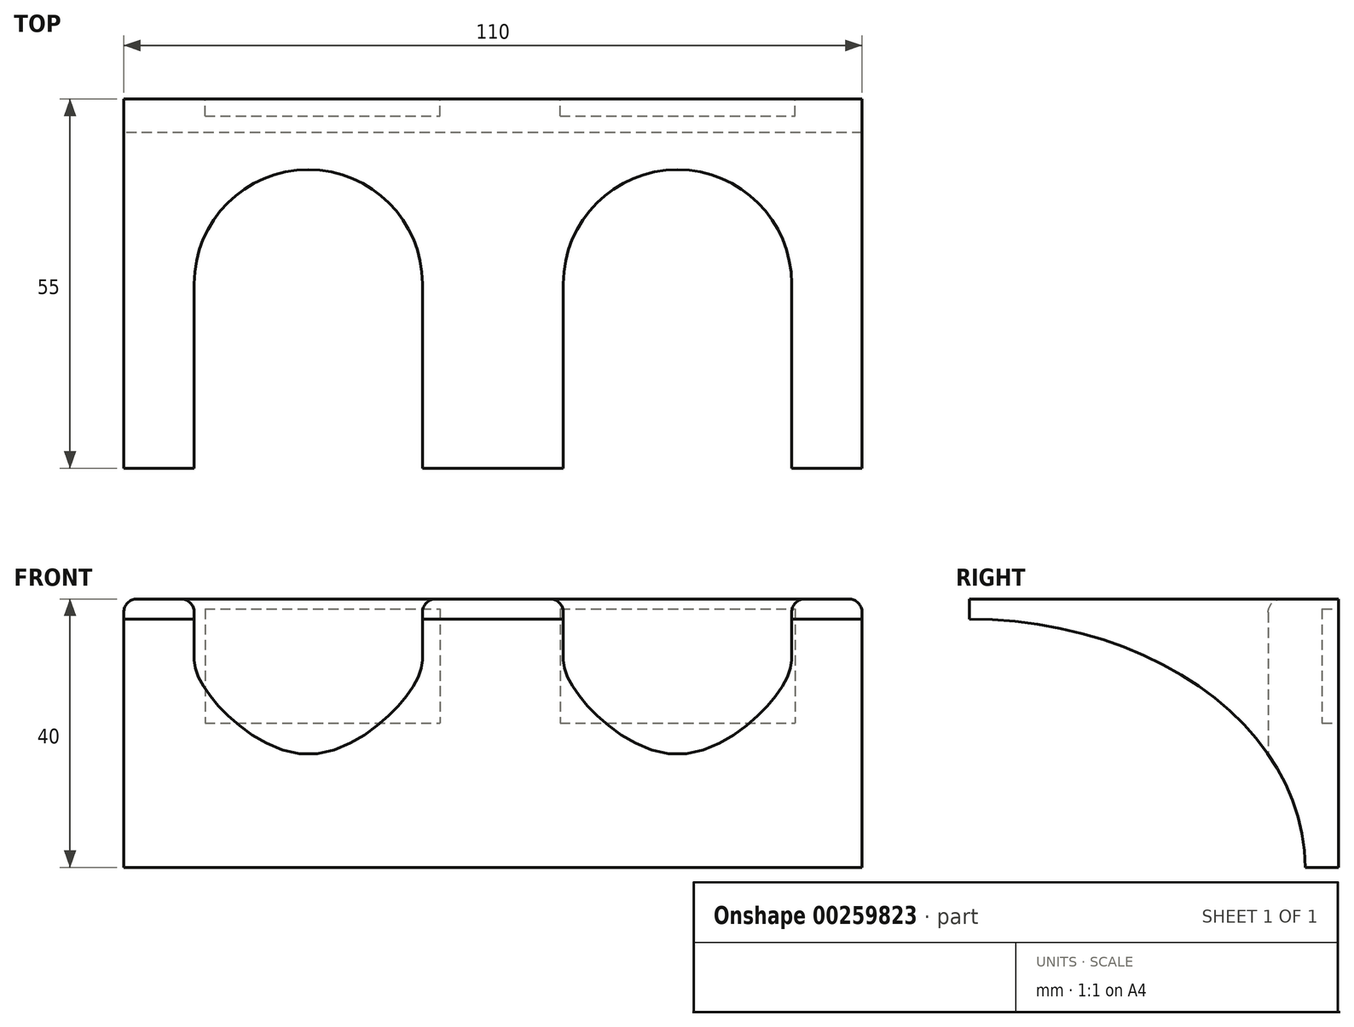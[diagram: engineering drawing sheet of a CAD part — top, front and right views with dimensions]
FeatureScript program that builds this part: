
annotation { "Feature Type Name" : "Feature", "Feature Type Description" : "" }
export const myFeature = defineFeature(function(context is Context, id is Id, definition is map)
    precondition{}
    {
        {
            var Q0;
            Q0=qCreatedBy(makeId("Top.planeOp"),FACE);
            var sketch = newSketch(context, id + "F0", { "sketchPlane" : qUnion([Q0])});
            skLineSegment(sketch, "E0.bottom", {"start": v(55, 27.5) * mm, "end": v(-55, 27.5) * mm});
            skLineSegment(sketch, "E0.top", {"start": v(55, -27.5) * mm, "end": v(-55, -27.5) * mm});
            skLineSegment(sketch, "E0.left", {"start": v(55, 27.5) * mm, "end": v(55, -27.5) * mm});
            skLineSegment(sketch, "E0.right", {"start": v(-55, 27.5) * mm, "end": v(-55, -27.5) * mm});
            skPoint(sketch, "E0.middle", {"position": v(0, 0) * mm});
            skLineSegment(sketch, "E1", {"start": v(0, 0) * mm, "end": v(-55, 0) * mm});
            skLineSegment(sketch, "E2", {"start": v(0, 0) * mm, "end": v(55, 0) * mm});
            skCircle(sketch, "E3", {"center": v(-27.5, 0) * mm, "radius": 17 * mm});
            skCircle(sketch, "E4", {"center": v(27.5, 0) * mm, "radius": 17 * mm});
            skLineSegment(sketch, "E5", {"start": v(-44.5, 0) * mm, "end": v(-44.5, -27.5) * mm});
            skLineSegment(sketch, "E6", {"start": v(-10.5, 0) * mm, "end": v(-10.5, -27.5) * mm});
            skLineSegment(sketch, "E7", {"start": v(10.5, 0) * mm, "end": v(10.5, -27.5) * mm});
            skLineSegment(sketch, "E8", {"start": v(44.5, 0) * mm, "end": v(44.5, -27.5) * mm});
            skSolve(sketch);
        }
        {
            var Q0;
            {var subQ3=sQuery(id+"F0.wireOp",EDGE,"E5");Q0=makeQuery(id+"F0.imprint","IMPRINT",FACE,{"disambiguationData":[TD([[makeQuery(id+"F0.imprint","IMPRINT",EDGE,{"derivedFrom":subQ3}),-1.0]])]});}
            var Q1;
            {var subQ6=sQuery(id+"F0.wireOp",EDGE,"E0.bottom");Q1=makeQuery(id+"F0.imprint","IMPRINT",FACE,{"disambiguationData":[TD([[makeQuery(id+"F0.imprint","IMPRINT",EDGE,{"derivedFrom":subQ6}),1.0]])]});}
            var Q2;
            {var subQ0=sQuery(id+"F0.wireOp",EDGE,"E6");Q2=makeQuery(id+"F0.imprint","IMPRINT",FACE,{"disambiguationData":[TD([[makeQuery(id+"F0.imprint","IMPRINT",EDGE,{"derivedFrom":subQ0}),1.0]])]});}
            var Q3;
            {var subQ3=sQuery(id+"F0.wireOp",EDGE,"E8");Q3=makeQuery(id+"F0.imprint","IMPRINT",FACE,{"disambiguationData":[TD([[makeQuery(id+"F0.imprint","IMPRINT",EDGE,{"derivedFrom":subQ3}),1.0]])]});}
            extrude(context, id + "F1", {"entities" : qUnion([Q0, Q1, Q2, Q3]), "depth" : 40 * mm});
        }
        {
            var Q0;
            Q0=makeQuery(id+"F1.opExtrude","SWEPT_FACE",FACE,{"disambiguationData":[OSD([sQuery(id+"F0.wireOp",EDGE,"E0.right")])]});
            var sketch = newSketch(context, id + "F2", { "sketchPlane" : qUnion([Q0])});
            skLineSegment(sketch, "E9", {"start": v(-27.5, 0) * mm, "end": v(-22.5, 0) * mm});
            skLineSegment(sketch, "E10", {"start": v(27.5, 40) * mm, "end": v(27.5, 37) * mm});
            skEllipse(sketch, "E11", {"center": v(27.5, 0) * mm, "majorRadius": 50 * mm, "minorRadius": 37 * mm, "majorAxis": v(-1, 0)});
            skSolve(sketch);
        }
        {
            var Q0;
            {var subQ1=sQuery(id+"F0.wireOp",EDGE,"E0.right");var subQ2=makeQuery(id+"F1.opExtrude","CAP_EDGE",EDGE,{"disambiguationData":[OSD([subQ1])],"isStart":true});var subQ4=makeQuery(id+"F1.opExtrude","SWEPT_EDGE",EDGE,{"disambiguationData":[OSD([sQuery(id+"F0.wireOp",EDGE,"E0.top"),subQ1])]});var subQ6=makeQuery(id+"F2.imprint","INTERSECT",VERTEX,{"derivedFrom":[subQ4,subQ2]});Q0=makeQuery(id+"F2.imprint","IMPRINT",FACE,{"disambiguationData":[TD([[makeQuery(id+"F2.imprint","IMPRINT",EDGE,{"disambiguationData":[TD([[subQ6,1.0]])],"derivedFrom":subQ2}),1.0]])]});}
            extrude(context, id + "F3", {"entities" : qUnion([Q0]), "operationType" : NewBodyOperationType.REMOVE, "oppositeDirection" : true, "depth" : 120.3 * mm});
        }
        {
            var Q0;
            Q0=makeQuery(id+"F1.opExtrude","SWEPT_FACE",FACE,{"disambiguationData":[OSD([sQuery(id+"F0.wireOp",EDGE,"E0.bottom")])]});
            var sketch = newSketch(context, id + "F4", { "sketchPlane" : qUnion([Q0])});
            skLineSegment(sketch, "E12", {"start": v(-55, 20) * mm, "end": v(0, 20) * mm});
            skLineSegment(sketch, "E13", {"start": v(0, 20) * mm, "end": v(50.8, 20) * mm});
            skPoint(sketch, "E13.endSnap0", {"position": v(55, 20) * mm});
            skLineSegment(sketch, "E14", {"start": v(-27.5, 20) * mm, "end": v(-27.5, 40) * mm});
            skLineSegment(sketch, "E15", {"start": v(25.4, 20) * mm, "end": v(25.4, 40) * mm});
            skLineSegment(sketch, "E16.bottom", {"start": v(-10, 38.5) * mm, "end": v(-45, 38.5) * mm});
            skLineSegment(sketch, "E16.top", {"start": v(-10, 21.5) * mm, "end": v(-45, 21.5) * mm});
            skLineSegment(sketch, "E16.left", {"start": v(-10, 38.5) * mm, "end": v(-10, 21.5) * mm});
            skLineSegment(sketch, "E16.right", {"start": v(-45, 38.5) * mm, "end": v(-45, 21.5) * mm});
            skPoint(sketch, "E16.middle", {"position": v(-27.5, 30) * mm});
            skLineSegment(sketch, "E17.bottom", {"start": v(42.9, 38.5) * mm, "end": v(7.9, 38.5) * mm});
            skLineSegment(sketch, "E17.top", {"start": v(42.9, 21.5) * mm, "end": v(7.9, 21.5) * mm});
            skLineSegment(sketch, "E17.left", {"start": v(42.9, 38.5) * mm, "end": v(42.9, 21.5) * mm});
            skLineSegment(sketch, "E17.right", {"start": v(7.9, 38.5) * mm, "end": v(7.9, 21.5) * mm});
            skPoint(sketch, "E17.middle", {"position": v(25.4, 30) * mm});
            skSolve(sketch);
        }
        {
            var Q0;
            {var subQ5=sQuery(id+"F4.wireOp",EDGE,"E16.right");Q0=makeQuery(id+"F4.imprint","IMPRINT",FACE,{"disambiguationData":[TD([[makeQuery(id+"F4.imprint","IMPRINT",EDGE,{"derivedFrom":subQ5}),1.0]])]});}
            var Q1;
            {var subQ5=sQuery(id+"F4.wireOp",EDGE,"E16.left");Q1=makeQuery(id+"F4.imprint","IMPRINT",FACE,{"disambiguationData":[TD([[makeQuery(id+"F4.imprint","IMPRINT",EDGE,{"derivedFrom":subQ5}),-1.0]])]});}
            var Q2;
            {var subQ5=sQuery(id+"F4.wireOp",EDGE,"E17.right");Q2=makeQuery(id+"F4.imprint","IMPRINT",FACE,{"disambiguationData":[TD([[makeQuery(id+"F4.imprint","IMPRINT",EDGE,{"derivedFrom":subQ5}),1.0]])]});}
            var Q3;
            {var subQ5=sQuery(id+"F4.wireOp",EDGE,"E17.left");Q3=makeQuery(id+"F4.imprint","IMPRINT",FACE,{"disambiguationData":[TD([[makeQuery(id+"F4.imprint","IMPRINT",EDGE,{"derivedFrom":subQ5}),-1.0]])]});}
            extrude(context, id + "F5", {"entities" : qUnion([Q0, Q1, Q2, Q3]), "operationType" : NewBodyOperationType.REMOVE, "oppositeDirection" : true, "depth" : 2.5 * mm});
        }
        {
            var Q0;
            Q0=makeQuery(id+"F1.opExtrude","CAP_EDGE",EDGE,{"disambiguationData":[OSD([sQuery(id+"F0.wireOp",EDGE,"E3")])],"isStart":false});
            var Q1;
            Q1=makeQuery(id+"F1.opExtrude","CAP_EDGE",EDGE,{"disambiguationData":[OSD([sQuery(id+"F0.wireOp",EDGE,"E4")])],"isStart":false});
            var Q2;
            Q2=makeQuery(id+"F1.opExtrude","CAP_EDGE",EDGE,{"disambiguationData":[OSD([sQuery(id+"F0.wireOp",EDGE,"E0.left")])],"isStart":false});
            var Q3;
            Q3=makeQuery(id+"F1.opExtrude","CAP_EDGE",EDGE,{"disambiguationData":[OSD([sQuery(id+"F0.wireOp",EDGE,"E0.right")])],"isStart":false});
            fillet(context, id + "F6", {"entities" : qUnion([Q0, Q1, Q2, Q3]), "radius" : 2 * mm, "tangentPropagation" : true, "allowEdgeOverflow" : false});
        }
    });
